# Revit family: F-03BTWT_v1.0 20241030
name_source: partatom
category: Communication Devices
units: mm (PartAtom-declared; Revit-internal decimal feet)

## family parameters
Always vertical = Yes
Cut with Voids When Loaded = No
Maintain Annotation Orientation = No
Part Type = Normal
Room Calculation Point = No
Round Connector Dimension = Use Diameter
Shared = No
Work Plane-Based = No

## types (4) — shared parameters
Depth = 132 mm  [stored 0.433071 ft]
Dimensions = 130(W) ×221(H)×132(D)mm
Height = 221 mm  [stored 0.725066 ft]
Manufacturer = TOA
Width = 130 mm  [stored 0.426509 ft]
バージョン = 1.0
zero-valued in all types: Default Elevation

## per-type parameters (varying)
- F-03B (Black, 8Ω): Accessory=スピーカー金具・・・ 1, ベース金具・・・1, ベース金具カバー... 1, 金具組立ねじ・ナット...式; Body=TOA-Body(Black); Enclosure=バスレフ型; Finish - Base bracket=圧延鋼板 t4.0 黒 (マンセルN1.0近似色) 塗装; Finish - Base bracket cover=HIPS 黒 (マンセルN1.0近似色); Finish - Enclosure=HIPS 黒 (マンセルN1.0近似色) 塗装; Finish - Grille=アルミ 黒 (マンセルN10近似色) 塗装; Finish - Speaker bracket=アルミダイカスト 黒 (マンセルN1.0近似色) 塗装; Grille=TOA-Grille(Black); Input Termina=プッシュターミナル; Instollation Environment=屋内; Model=F-03B; Operoting Temperature=-10°C~+50°C; Oprion - Adapter plate=HY-F03B; Option - Speaker Stando=ST-34B 設置にはK&M社製アダプター 19780もしくは19610が必要です。; Product Info=https://www.toa.jp; Rated Impedance (100V line)=8 Ω; Rated Impedance (70V line)=670 Ω (15 W), 2 kΩ (5 W), 3.3 kΩ (3 W), 10 kΩ (1 W); Rated Impedance (Low)=8Ω; Rated Input=定格ノイズ:30W/連続プログラム:60W; Speaker Component=25mmドームツイーター; URL=https://www.toa-products.com; Update Info=https://www.toa-products.com; Weight=1.2kg
- F-03BM (Black, Hi-Z): Accessory=スピーカー金具・・・ 1, ベース金具 ・・・ 1, ベース金具カバー... 1, 金具組立ねじ・ナット・・・一式; Body=TOA-Body(Black); Crossover Frequency=M級(消防法施行規則 音声警報音第2シグナルでの測定で87 dB(A)以上); Directivty Angle=L級 (消防法施行規則 音声警報音第2シグナルでの測定で92dB(A)以上); Enclosure=バスレフ型; Finish - Base bracket=圧延鋼板 t4.0 黒 (マンセルN1.0近似色) 塗装; Finish - Base bracket cover=HIPS 黒 (マンセルN1.0近似色); Finish - Enclosure=HIPS 黒 (マンセルN1.0近似色) 塗装; Finish - Grille=アルミ 黒 (マンセルN10近似色) 塗装; Finish - Speaker bracket=アルミダイカスト 黒 (マンセルN1.0近似色) 塗装; Frequency Response=S級(消防法施行規則 音声警報音第2シグナルでの測定で84 dB(A)以上); Grille=TOA-Grille(Black); Input Termina=プッシュターミナル; Instollation Environment=屋内; Model=F-03BM; Operoting Temperature=-10°C~+50°C; Oprion - Adapter plate=HY-F03B; Option - Speaker Stando=ST-34B 設置にはK&M社製アダプター 19780もしくは19610が必要です。; Power Handling Capacity=15W; Product Info=https://www.toa.jp; Rated Impedance (100V line)=8 Ω; Rated Impedance (70V line)=670 Ω (15 W), 2 kΩ (5 W), 3.3 kΩ (3 W), 10 kΩ (1 W); Rated Impedance (Low)=670Ω (15W), 2kΩ (5W), 3.3kΩ (3W), 10kΩ (1W); Speaker Component=25mmドームツイーター; URL=https://www.toa-products.com; Update Info=https://www.toa-products.com; Weight=1.7kg
- F-03WT (White): Accessory=Speaker bracket ···1, Base bracket ···1, Base bracket cover ···1, Bracket fixing screw ···1 set; Body=TOA-Body(White); Crossover Frequency=4.5kHz; Directivty Angle=Horizontal: 100°, Vertical: 100°; Enclosure=Bass-reflex type; Finish - Base bracket=Steel plate, t4, white (RAL 9016 equivalent), paint; Finish - Base bracket cover=HIPS, white (RAL 9016 equivalent; Finish - Enclosure=HIPS, white (RAL 9016 equivalent), pain; Finish - Grille=Aluminum, white (RAL 9016 equivalent), paint; Finish - Speaker bracket=Die-cast aluminum, white (RAL 9016 equivalent), paint Base; Frequency Response=85 Hz - 20 kHz, -10 dB at installation in 1 /2 free sound field; Grille=TOA-Grille(White); Input Termina=Push-in termina; Instollation Environment=Indoor installation; Model=F-03WT; Operoting Temperature=-10 °C to +50 °C (14 °F to 122 °F); Oprion - Adapter plate=HY-F03W; Option - Speaker Stando=ST-34B Note: K&M 19780 or K&M 19610 is required.; Power Handling Capacity=Rated noise power: 30 W (8 Ω), Continuous program: 60 W (8 Ω); Product Info=https://www.toa-products.com; Rated Impedance (100V line)=670 Ω (15 W), 2 kΩ (5 W), 3.3 kΩ (3 W), 10 kΩ (1 W); Rated Impedance (70V line)=330 Ω (15 W), 670 Ω (7.5 W), 2 kΩ (2.5 W), 3.3 kΩ (1.5 W), 10 kΩ (0.5 W); Rated Impedance (Low)=8 Ω; Rated Input=15 W (100 V line, 70 V line); Sensitivty=87 dB (1 W, 1 m) at installation in 1/2 free sound field; Speaker Component=9 cm (3.5") Full-range PPcone-type; URL=https://www.toa.jp; Update Info=https://www.sound-toa.com; Weight=1.7 kg (3.75 lb)
- F-03WM (White, Hi-Z): Accessory=スピーカー金具・・・ 1, ベース金具 ・・・ 1, ベース金具カバー... 1, 金具組立ねじ・ナット・・・一式; Body=TOA-Body(White); Crossover Frequency=M級(消防法施行規則 音声警報音第2シグナルでの測定で87 dB(A)以上); Directivty Angle=L級 (消防法施行規則 音声警報音第2シグナルでの測定で92dB(A)以上); Enclosure=バスレフ型; Finish - Base bracket=圧延鋼板 t4.0 ホワイト (マンセルN9.3近似色) 塗装; Finish - Base bracket cover=HIPS ホワイト (マンセルN9.3近似色); Finish - Enclosure=HIPS ホワイト (マンセルN9.3近似色) 塗装; Finish - Grille=アルミ ホワイト (マンセルN9.3近似色) 塗装; Finish - Speaker bracket=アルミダイカスト ホワイト (マンセルN9.3近似色) 塗装; Frequency Response=S級(消防法施行規則 音声警報音第2シグナルでの測定で84 dB(A)以上); Grille=TOA-Grille(White); Input Termina=プッシュターミナル; Instollation Environment=屋内; Model=F-03WM; Operoting Temperature=-10°C~+50°C; Oprion - Adapter plate=HY-F03W; Option - Speaker Stando=ST-34B 設置にはK&M社製アダプター 19780もしくは19610が必要です。; Power Handling Capacity=15W; Product Info=https://www.toa.jp; Rated Impedance (100V line)=8 Ω; Rated Impedance (70V line)=670 Ω (15 W), 2 kΩ (5 W), 3.3 kΩ (3 W), 10 kΩ (1 W); Rated Impedance (Low)=670Ω (15W), 2kΩ (5W), 3.3kΩ (3W), 10kΩ (1W); Speaker Component=25mmドームツイーター; URL=https://www.toa-products.com; Update Info=https://www.toa-products.com; Weight=1.7kg

note: [stored X ft] marks values corroborated as IEEE doubles in the binary element streams (Revit-internal decimal feet)
